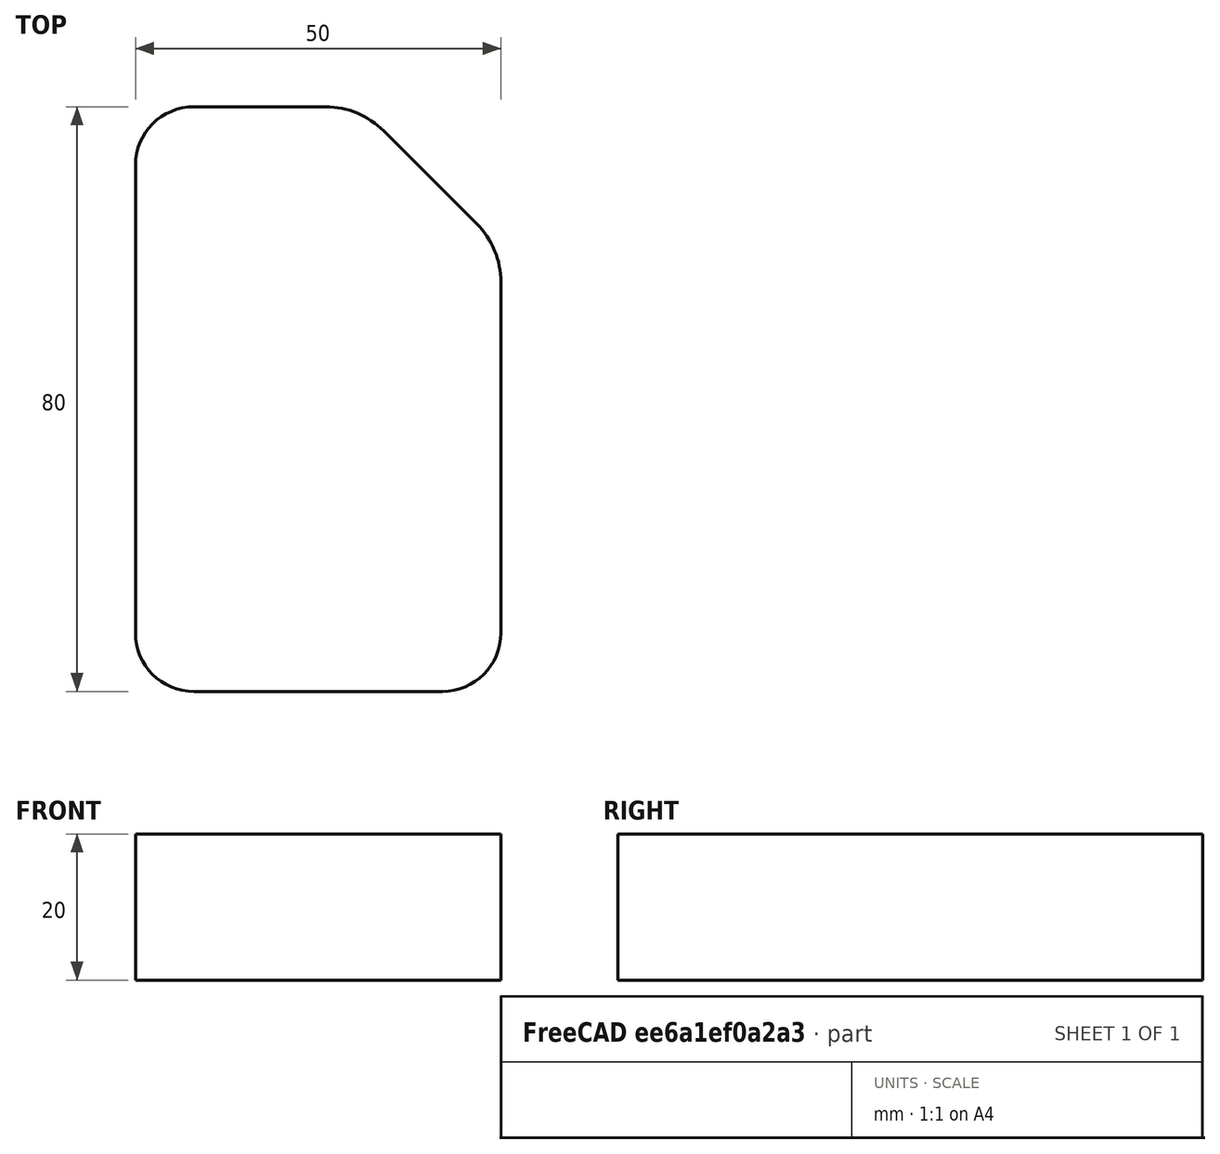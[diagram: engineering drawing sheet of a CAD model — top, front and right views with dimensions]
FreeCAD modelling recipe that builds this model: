
FCSTD DOCUMENT
Label: DualCellModv1
objects: Sketcher::SketchObject×1, PartDesign::Pad×1
note: 3 computed .brp shape members not serialized (recipe doc carries the construction recipe); baked Part::Feature solids carry a one-line shape summary decoded from their .brp

FEATURE [Sketcher::SketchObject] Sketch
  sketch-geometry (10):
    g0: LineSegment StartX=50 StartY=7.99998 StartZ=0 EndX=50 EndY=56 EndZ=0
    g1: LineSegment StartX=0 StartY=72 StartZ=0 EndX=0 EndY=8 EndZ=0
    g2: LineSegment StartX=8 StartY=80 StartZ=0 EndX=26 EndY=80 EndZ=0
    g3: LineSegment StartX=8 StartY=0 StartZ=0 EndX=42 EndY=0 EndZ=0
    g4: ArcOfCircle CenterX=8 CenterY=72 CenterZ=0 NormalX=0 NormalY=0 NormalZ=1 Radius=8 StartAngle=1.5708 EndAngle=3.14159
    g5: ArcOfCircle CenterX=42 CenterY=8 CenterZ=0 NormalX=0 NormalY=0 NormalZ=1 Radius=8 StartAngle=4.71239 EndAngle=6.28318
    g6: ArcOfCircle CenterX=8 CenterY=8 CenterZ=0 NormalX=0 NormalY=0 NormalZ=1 Radius=8 StartAngle=3.14159 EndAngle=4.71239
    g7: LineSegment StartX=33.9706 StartY=76.6985 StartZ=0 EndX=46.6985 EndY=63.9706 EndZ=0
    g8: ArcOfCircle CenterX=26 CenterY=68.7279 CenterZ=0 NormalX=0 NormalY=0 NormalZ=1 Radius=11.2721 StartAngle=0.785402 EndAngle=1.5708
    g9: ArcOfCircle CenterX=38.7279 CenterY=56 CenterZ=0 NormalX=0 NormalY=0 NormalZ=1 Radius=11.2721 StartAngle=2.7067e-08 EndAngle=0.785398
  constraints (35):
    c: Vertical(g0)
    c: Vertical(g1)
    c: Horizontal(g2)
    c: Horizontal(g3)
    c: Coincident(g6,g1)
    c: Coincident(g3,g6)
    c: Coincident(g3,g5)
    c: Coincident(g5,g0)
    c: Coincident(g2,g4)
    c: Coincident(g1,g4)
    c: Radius(g4) = 8
    c: Equal(g5,g6)
    c: DistanceY(g2,g3) = -80
    c: Tangent(g4,g2)
    c: Tangent(g5,g3)
    c: DistanceX(g1,g0) = 50
    c: DistanceX(g1) = 0
    c: Tangent(g1,g4)
    c: Tangent(g3,g6)
    c: Tangent(g6,g1)
    c: DistanceY(g3) = 0
    c: Angle(g7) = -0.785398
    c: Coincident(g7,g8)
    c: Coincident(g8,g2)
    c: Tangent(g8,g2)
    c: Tangent(g7,g8)
    c: Coincident(g9,g7)
    c: Tangent(g9,g7)
    c: Coincident(g9,g0)
    c: Distance(g7) = 18
    c: Distance(g2) = 18
    c: Equal(g9,g8)
    c: Equal(g4,g6)
    c: Tangent(g0,g9)
    c: Tangent(g5,g0)
FEATURE [PartDesign::Pad] Pad
  Length = 20
  MirroredExtent = false
  Sketch = -> Sketch
